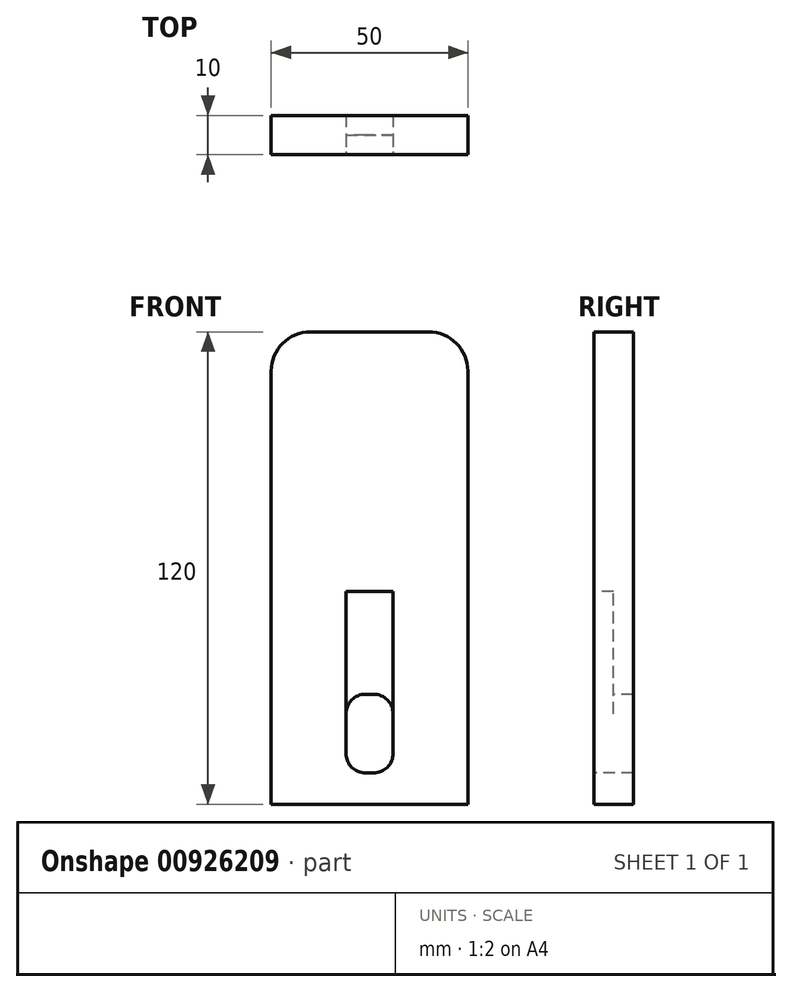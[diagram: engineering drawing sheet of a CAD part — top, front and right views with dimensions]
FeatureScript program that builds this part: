
annotation { "Feature Type Name" : "Feature", "Feature Type Description" : "" }
export const myFeature = defineFeature(function(context is Context, id is Id, definition is map)
    precondition{}
    {
        {
            var Q0;
            Q0=qCreatedBy(makeId("Front.planeOp"),FACE);
            var sketch = newSketch(context, id + "F0", { "sketchPlane" : qUnion([Q0])});
            skLineSegment(sketch, "E0.bottom", {"start": v(15, 60) * mm, "end": v(-15, 60) * mm});
            skLineSegment(sketch, "E0.top", {"start": v(25, -60) * mm, "end": v(-25, -60) * mm});
            skLineSegment(sketch, "E0.left", {"start": v(25, 50) * mm, "end": v(25, -60) * mm});
            skLineSegment(sketch, "E0.right", {"start": v(-25, 50) * mm, "end": v(-25, -60) * mm});
            skPoint(sketch, "E0.middle", {"position": v(0, 0) * mm});
            skPoint(sketch, "E1.visualSharp", {"position": v(-25, 60) * mm});
            skArc(sketch, "E1.filletArc", {"start": v(-15, 60) * mm, "mid": v(-22.07, 57.07) * mm, "end": v(-25, 50) * mm});
            skPoint(sketch, "E2.visualSharp", {"position": v(25, 60) * mm});
            skArc(sketch, "E2.filletArc", {"start": v(25, 50) * mm, "mid": v(22.07, 57.07) * mm, "end": v(15, 60) * mm});
            skSolve(sketch);
        }
        {
            var Q0;
            Q0 = qSketchRegion(id + "F0", true);
            extrude(context, id + "F1", {"entities" : qUnion([Q0]), "depth" : 10 * mm, "offsetDistance" : 25.4 * mm});
        }
        {
            var Q0;
            Q0=makeQuery(id+"F1.opExtrude","CAP_FACE",FACE,{"disambiguationData":[OSD([sQuery(id+"F0.wireOp",EDGE,"E0.bottom"),sQuery(id+"F0.wireOp",EDGE,"E0.top"),sQuery(id+"F0.wireOp",EDGE,"E0.left"),sQuery(id+"F0.wireOp",EDGE,"E0.right"),sQuery(id+"F0.wireOp",EDGE,"E1.filletArc"),sQuery(id+"F0.wireOp",EDGE,"E2.filletArc")])],"isStart":false});
            var sketch = newSketch(context, id + "F2", { "sketchPlane" : qUnion([Q0])});
            skLineSegment(sketch, "E3.bottom", {"start": v(-1, -32.07) * mm, "end": v(1, -32.07) * mm});
            skLineSegment(sketch, "E3.top", {"start": v(-1, -52.07) * mm, "end": v(1, -52.07) * mm});
            skLineSegment(sketch, "E3.left", {"start": v(-6, -37.07) * mm, "end": v(-6, -47.07) * mm});
            skLineSegment(sketch, "E3.right", {"start": v(6, -37.07) * mm, "end": v(6, -47.07) * mm});
            skPoint(sketch, "E4.visualSharp", {"position": v(-6, -32.07) * mm});
            skArc(sketch, "E4.filletArc", {"start": v(-1, -32.07) * mm, "mid": v(-4.54, -33.54) * mm, "end": v(-6, -37.07) * mm});
            skPoint(sketch, "E5.visualSharp", {"position": v(6, -32.07) * mm});
            skArc(sketch, "E5.filletArc", {"start": v(6, -37.07) * mm, "mid": v(4.54, -33.54) * mm, "end": v(1, -32.07) * mm});
            skPoint(sketch, "E6.visualSharp", {"position": v(6, -52.07) * mm});
            skArc(sketch, "E6.filletArc", {"start": v(1, -52.07) * mm, "mid": v(4.54, -50.6) * mm, "end": v(6, -47.07) * mm});
            skPoint(sketch, "E7.visualSharp", {"position": v(-6, -52.07) * mm});
            skArc(sketch, "E7.filletArc", {"start": v(-6, -47.07) * mm, "mid": v(-4.54, -50.6) * mm, "end": v(-1, -52.07) * mm});
            skSolve(sketch);
        }
        {
            var Q0;
            Q0 = qSketchRegion(id + "F2", true);
            extrude(context, id + "F3", {"entities" : qUnion([Q0]), "operationType" : NewBodyOperationType.REMOVE, "oppositeDirection" : true, "depth" : 11 * mm, "offsetDistance" : 25.4 * mm});
        }
        {
            var Q0;
            Q0=makeQuery(id+"F1.opExtrude","CAP_FACE",FACE,{"disambiguationData":[OSD([sQuery(id+"F0.wireOp",EDGE,"E0.bottom"),sQuery(id+"F0.wireOp",EDGE,"E0.top"),sQuery(id+"F0.wireOp",EDGE,"E0.left"),sQuery(id+"F0.wireOp",EDGE,"E0.right"),sQuery(id+"F0.wireOp",EDGE,"E1.filletArc"),sQuery(id+"F0.wireOp",EDGE,"E2.filletArc")])],"isStart":false});
            var sketch = newSketch(context, id + "F4", { "sketchPlane" : qUnion([Q0])});
            skLineSegment(sketch, "E8.bottom", {"start": v(-6, -39.18) * mm, "end": v(6, -39.18) * mm});
            skLineSegment(sketch, "E8.top", {"start": v(-6, -6) * mm, "end": v(6, -6) * mm});
            skLineSegment(sketch, "E8.left", {"start": v(-6, -39.18) * mm, "end": v(-6, -6) * mm});
            skLineSegment(sketch, "E8.right", {"start": v(6, -39.18) * mm, "end": v(6, -6) * mm});
            skSolve(sketch);
        }
        {
            var Q0;
            Q0 = qSketchRegion(id + "F4", true);
            extrude(context, id + "F5", {"entities" : qUnion([Q0]), "operationType" : NewBodyOperationType.REMOVE, "oppositeDirection" : true, "depth" : 5 * mm, "offsetDistance" : 25.4 * mm});
        }
    });
